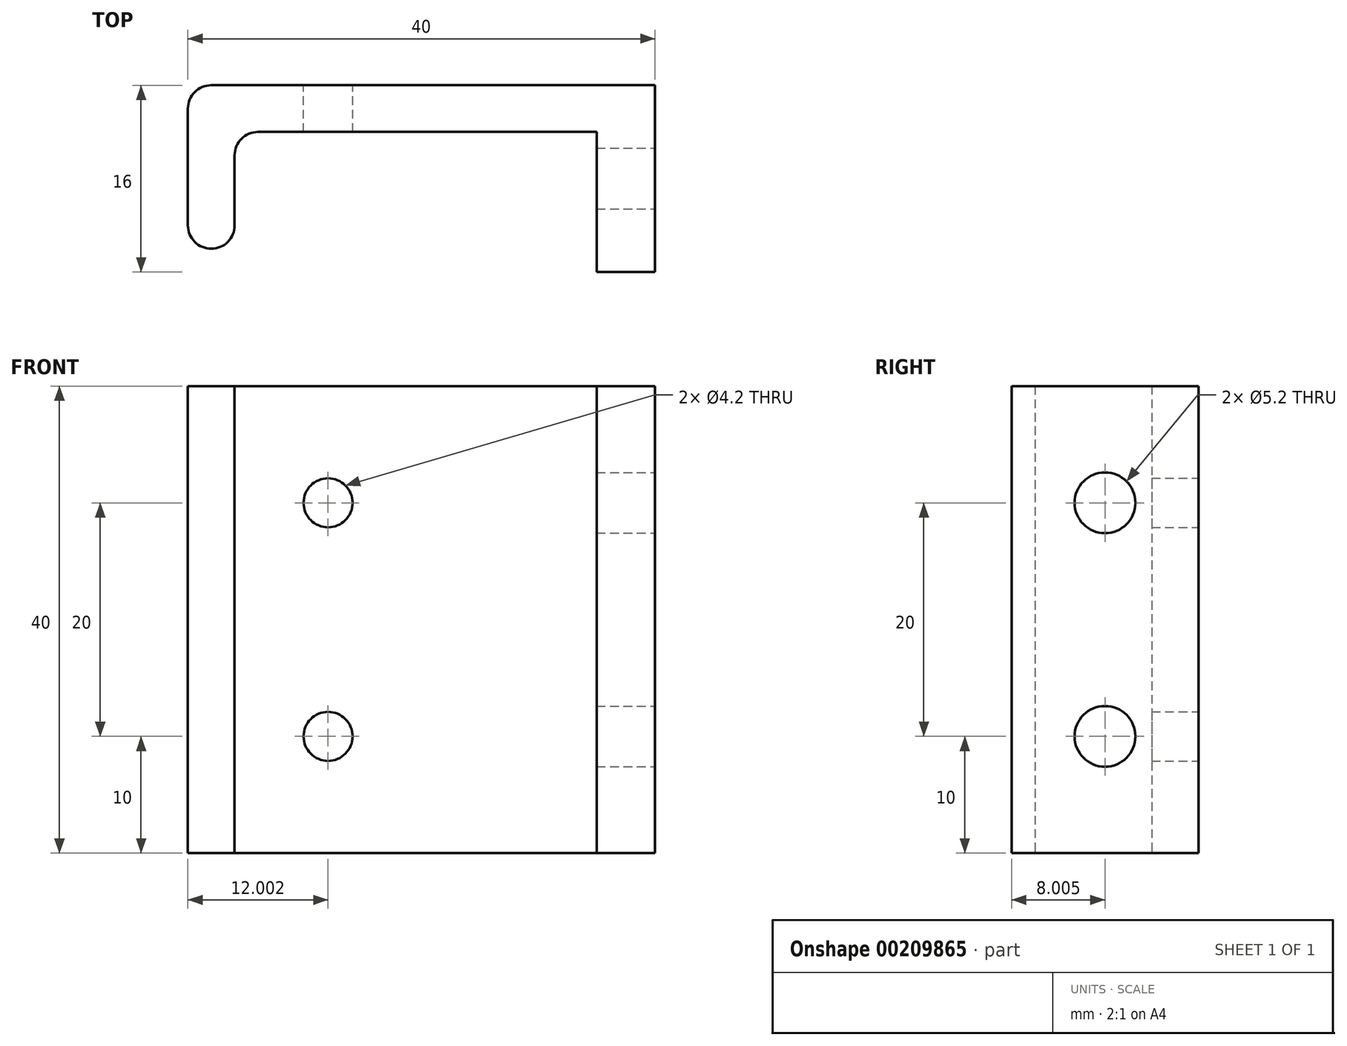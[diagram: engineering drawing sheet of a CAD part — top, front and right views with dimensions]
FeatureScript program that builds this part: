
annotation { "Feature Type Name" : "Feature", "Feature Type Description" : "" }
export const myFeature = defineFeature(function(context is Context, id is Id, definition is map)
    precondition{}
    {
        {
            var Q0;
            Q0=qCreatedBy(makeId("Top.planeOp"),FACE);
            var sketch = newSketch(context, id + "F0", { "sketchPlane" : qUnion([Q0])});
            skLineSegment(sketch, "E0.bottom", {"start": v(-76.57, 36.2) * mm, "end": v(-36.57, 36.2) * mm});
            skLineSegment(sketch, "E0.top", {"start": v(-76.57, 32.2) * mm, "end": v(-36.57, 32.2) * mm});
            skLineSegment(sketch, "E0.left", {"start": v(-76.57, 36.2) * mm, "end": v(-76.57, 32.2) * mm});
            skLineSegment(sketch, "E0.right", {"start": v(-36.57, 36.2) * mm, "end": v(-36.57, 32.2) * mm});
            skLineSegment(sketch, "E1.bottom", {"start": v(-41.57, 32.2) * mm, "end": v(-36.57, 32.2) * mm});
            skLineSegment(sketch, "E1.top", {"start": v(-41.57, 20.2) * mm, "end": v(-36.57, 20.2) * mm});
            skLineSegment(sketch, "E1.left", {"start": v(-41.57, 32.2) * mm, "end": v(-41.57, 20.2) * mm});
            skLineSegment(sketch, "E1.right", {"start": v(-36.57, 32.2) * mm, "end": v(-36.57, 20.2) * mm});
            skLineSegment(sketch, "E2.bottom", {"start": v(-76.57, 32.2) * mm, "end": v(-72.57, 32.2) * mm});
            skLineSegment(sketch, "E2.top", {"start": v(-76.57, 22.2) * mm, "end": v(-72.57, 22.2) * mm});
            skLineSegment(sketch, "E2.left", {"start": v(-76.57, 32.2) * mm, "end": v(-76.57, 22.2) * mm});
            skLineSegment(sketch, "E2.right", {"start": v(-72.57, 32.2) * mm, "end": v(-72.57, 22.2) * mm});
            skSolve(sketch);
        }
        {
            var Q0;
            Q0 = qSketchRegion(id + "F0", true);
            extrude(context, id + "F1", {"entities" : qUnion([Q0]), "depth" : 40 * mm});
        }
        {
            var Q0;
            Q0=makeQuery(id+"F1.opExtrude","SWEPT_FACE",FACE,{"disambiguationData":[OSD([sQuery(id+"F0.wireOp",EDGE,"E0.right"),sQuery(id+"F0.wireOp",EDGE,"E1.right")])]});
            var sketch = newSketch(context, id + "F2", { "sketchPlane" : qUnion([Q0])});
            skPoint(sketch, "E3", {"position": v(28.2, 30) * mm});
            skPoint(sketch, "E4", {"position": v(28.2, 10) * mm});
            skSolve(sketch);
        }
        {
            var Q0;
            Q0=makeQuery(id+"F1.opExtrude","SWEPT_EDGE",EDGE,{"disambiguationData":[OSD([sQuery(id+"F0.wireOp",EDGE,"E0.bottom"),sQuery(id+"F0.wireOp",EDGE,"E0.left")])]});
            var Q1;
            Q1=makeQuery(id+"F1.opExtrude","SWEPT_EDGE",EDGE,{"disambiguationData":[OSD([sQuery(id+"F0.wireOp",EDGE,"E0.top"),sQuery(id+"F0.wireOp",EDGE,"E2.bottom"),sQuery(id+"F0.wireOp",EDGE,"E2.right")])]});
            var Q2;
            Q2=makeQuery(id+"F1.opExtrude","SWEPT_EDGE",EDGE,{"disambiguationData":[OSD([sQuery(id+"F0.wireOp",EDGE,"E2.top"),sQuery(id+"F0.wireOp",EDGE,"E2.left")])]});
            var Q3;
            Q3=makeQuery(id+"F1.opExtrude","SWEPT_EDGE",EDGE,{"disambiguationData":[OSD([sQuery(id+"F0.wireOp",EDGE,"E2.top"),sQuery(id+"F0.wireOp",EDGE,"E2.right")])]});
            fillet(context, id + "F3", {"entities" : qUnion([Q0, Q1, Q2, Q3]), "radius" : 2 * mm, "tangentPropagation" : true, "allowEdgeOverflow" : false});
        }
        {
            var Q0;
            Q0=sQuery(id+"F2.wireOp",VERTEX,"E4");
            var Q1;
            Q1=sQuery(id+"F2.wireOp",VERTEX,"E3");
            var Q2;
            Q2=makeQuery(id+"F1.opExtrude","SWEPT_BODY",BODY,{"disambiguationData":[OSD([sQuery(id+"F0.wireOp",EDGE,"E0.bottom"),sQuery(id+"F0.wireOp",EDGE,"E0.top"),sQuery(id+"F0.wireOp",EDGE,"E0.left"),sQuery(id+"F0.wireOp",EDGE,"E0.right"),sQuery(id+"F0.wireOp",EDGE,"E1.top"),sQuery(id+"F0.wireOp",EDGE,"E1.left"),sQuery(id+"F0.wireOp",EDGE,"E1.right"),sQuery(id+"F0.wireOp",EDGE,"E2.top"),sQuery(id+"F0.wireOp",EDGE,"E2.left"),sQuery(id+"F0.wireOp",EDGE,"E2.right")])]});
            hole(context, id + "F4", {"style" : HoleStyle.SIMPLE, "endStyle" : HoleEndStyle.BLIND, "holeDiameter" : 5.2 * mm, "holeDepth" : 12 * mm, "tappedDepth" : 12 * mm, "tapClearance" : 3, "locations" : qUnion([Q0, Q1]), "scope" : qUnion([Q2])});
        }
        {
            var Q0;
            Q0=makeQuery(id+"F1.opExtrude","SWEPT_FACE",FACE,{"disambiguationData":[OSD([sQuery(id+"F0.wireOp",EDGE,"E0.bottom")])]});
            var sketch = newSketch(context, id + "F5", { "sketchPlane" : qUnion([Q0])});
            skPoint(sketch, "E5", {"position": v(64.57, 10) * mm});
            skPoint(sketch, "E6", {"position": v(64.57, 30) * mm});
            skSolve(sketch);
        }
        {
            var Q0;
            Q0=sQuery(id+"F5.wireOp",VERTEX,"E5");
            var Q1;
            Q1=sQuery(id+"F5.wireOp",VERTEX,"E6");
            var Q2;
            Q2=makeQuery(id+"F1.opExtrude","SWEPT_BODY",BODY,{"disambiguationData":[OSD([sQuery(id+"F0.wireOp",EDGE,"E0.bottom"),sQuery(id+"F0.wireOp",EDGE,"E0.top"),sQuery(id+"F0.wireOp",EDGE,"E0.left"),sQuery(id+"F0.wireOp",EDGE,"E0.right"),sQuery(id+"F0.wireOp",EDGE,"E1.top"),sQuery(id+"F0.wireOp",EDGE,"E1.left"),sQuery(id+"F0.wireOp",EDGE,"E1.right"),sQuery(id+"F0.wireOp",EDGE,"E2.top"),sQuery(id+"F0.wireOp",EDGE,"E2.left"),sQuery(id+"F0.wireOp",EDGE,"E2.right")])]});
            hole(context, id + "F6", {"style" : HoleStyle.SIMPLE, "endStyle" : HoleEndStyle.BLIND, "holeDiameter" : 4.2 * mm, "holeDepth" : 12 * mm, "tappedDepth" : 12 * mm, "tapClearance" : 3, "locations" : qUnion([Q0, Q1]), "scope" : qUnion([Q2])});
        }
    });
